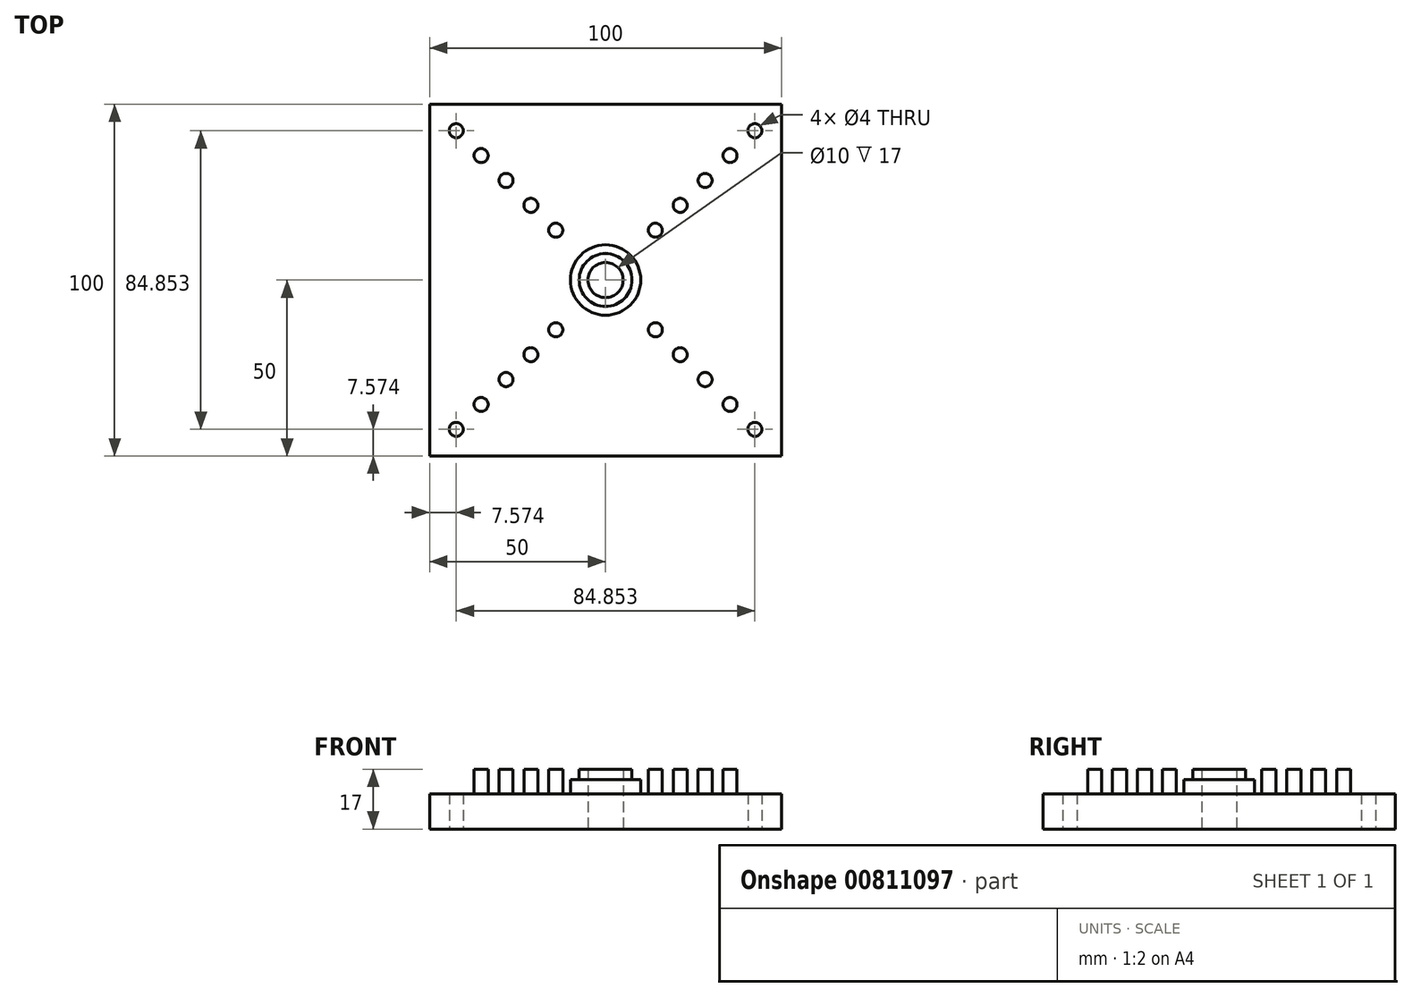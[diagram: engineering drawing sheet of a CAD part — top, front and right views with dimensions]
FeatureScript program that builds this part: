
annotation { "Feature Type Name" : "Feature", "Feature Type Description" : "" }
export const myFeature = defineFeature(function(context is Context, id is Id, definition is map)
    precondition{}
    {
        {
            var Q0;
            Q0=qCreatedBy(makeId("Top.planeOp"),FACE);
            var sketch = newSketch(context, id + "F0", { "sketchPlane" : qUnion([Q0])});
            skLineSegment(sketch, "E0.bottom", {"start": v(50, -50) * mm, "end": v(-50, -50) * mm});
            skLineSegment(sketch, "E0.top", {"start": v(50, 50) * mm, "end": v(-50, 50) * mm});
            skLineSegment(sketch, "E0.left", {"start": v(50, -50) * mm, "end": v(50, 50) * mm});
            skLineSegment(sketch, "E0.right", {"start": v(-50, -50) * mm, "end": v(-50, 50) * mm});
            skPoint(sketch, "E0.middle", {"position": v(0, 0) * mm});
            skLineSegment(sketch, "E1", {"start": v(0, 0) * mm, "end": v(42.43, -42.43) * mm, "construction": true});
            skLineSegment(sketch, "E2", {"start": v(42.43, -42.43) * mm, "end": v(50, -50) * mm, "construction": true});
            skCircle(sketch, "E3", {"center": v(42.43, -42.43) * mm, "radius": 2 * mm});
            skCircle(sketch, "E4.1.0", {"center": v(42.43, 42.43) * mm, "radius": 2 * mm});
            skCircle(sketch, "E4.2.0", {"center": v(-42.43, 42.43) * mm, "radius": 2 * mm});
            skCircle(sketch, "E4.3.0", {"center": v(-42.43, -42.43) * mm, "radius": 2 * mm});
            skSolve(sketch);
        }
        {
            var Q0;
            Q0 = qSketchRegion(id + "F0", true);
            extrude(context, id + "F1", {"entities" : qUnion([Q0]), "depth" : 10 * mm, "offsetDistance" : 25 * mm});
        }
        {
            var Q0;
            Q0=makeQuery(id+"F1.opExtrude","CAP_FACE",FACE,{"disambiguationData":[OSD([sQuery(id+"F0.wireOp",EDGE,"E0.bottom"),sQuery(id+"F0.wireOp",EDGE,"E0.top"),sQuery(id+"F0.wireOp",EDGE,"E0.left"),sQuery(id+"F0.wireOp",EDGE,"E0.right"),sQuery(id+"F0.wireOp",EDGE,"E3"),sQuery(id+"F0.wireOp",EDGE,"E4.1.0"),sQuery(id+"F0.wireOp",EDGE,"E4.2.0"),sQuery(id+"F0.wireOp",EDGE,"E4.3.0")])],"isStart":false});
            var sketch = newSketch(context, id + "F2", { "sketchPlane" : qUnion([Q0])});
            skLineSegment(sketch, "E5", {"start": v(0, 0) * mm, "end": v(14.14, -14.14) * mm, "construction": true});
            skLineSegment(sketch, "E6", {"start": v(28.28, -28.28) * mm, "end": v(35.36, -35.36) * mm, "construction": true});
            skLineSegment(sketch, "E7", {"start": v(21.21, -21.21) * mm, "end": v(28.28, -28.28) * mm, "construction": true});
            skLineSegment(sketch, "E8", {"start": v(14.14, -14.14) * mm, "end": v(21.21, -21.21) * mm, "construction": true});
            skLineSegment(sketch, "E9", {"start": v(35.36, -35.36) * mm, "end": v(42.43, -42.43) * mm, "construction": true});
            skCircle(sketch, "E10", {"center": v(14.14, -14.14) * mm, "radius": 2 * mm});
            skCircle(sketch, "E11", {"center": v(21.21, -21.21) * mm, "radius": 2 * mm});
            skCircle(sketch, "E12", {"center": v(28.28, -28.28) * mm, "radius": 2 * mm});
            skCircle(sketch, "E13", {"center": v(35.36, -35.36) * mm, "radius": 2 * mm});
            skCircle(sketch, "E14.1.0", {"center": v(14.14, 14.14) * mm, "radius": 2 * mm});
            skCircle(sketch, "E14.1.1", {"center": v(21.21, 21.21) * mm, "radius": 2 * mm});
            skCircle(sketch, "E14.1.2", {"center": v(28.28, 28.28) * mm, "radius": 2 * mm});
            skCircle(sketch, "E14.1.3", {"center": v(35.36, 35.36) * mm, "radius": 2 * mm});
            skCircle(sketch, "E14.2.0", {"center": v(-14.14, 14.14) * mm, "radius": 2 * mm});
            skCircle(sketch, "E14.2.1", {"center": v(-21.21, 21.21) * mm, "radius": 2 * mm});
            skCircle(sketch, "E14.2.2", {"center": v(-28.28, 28.28) * mm, "radius": 2 * mm});
            skCircle(sketch, "E14.2.3", {"center": v(-35.36, 35.36) * mm, "radius": 2 * mm});
            skCircle(sketch, "E14.3.0", {"center": v(-14.14, -14.14) * mm, "radius": 2 * mm});
            skCircle(sketch, "E14.3.1", {"center": v(-21.21, -21.21) * mm, "radius": 2 * mm});
            skCircle(sketch, "E14.3.2", {"center": v(-28.28, -28.28) * mm, "radius": 2 * mm});
            skCircle(sketch, "E14.3.3", {"center": v(-35.36, -35.36) * mm, "radius": 2 * mm});
            skPoint(sketch, "E14.center", {"position": v(0, 0) * mm});
            skSolve(sketch);
        }
        {
            var Q0;
            Q0 = qSketchRegion(id + "F2", true);
            extrude(context, id + "F3", {"entities" : qUnion([Q0]), "operationType" : NewBodyOperationType.ADD, "depth" : 7 * mm, "offsetDistance" : 25 * mm});
        }
        {
            var Q0;
            Q0=makeQuery(id+"F1.opExtrude","CAP_FACE",FACE,{"disambiguationData":[OSD([sQuery(id+"F0.wireOp",EDGE,"E0.bottom"),sQuery(id+"F0.wireOp",EDGE,"E0.top"),sQuery(id+"F0.wireOp",EDGE,"E0.left"),sQuery(id+"F0.wireOp",EDGE,"E0.right"),sQuery(id+"F0.wireOp",EDGE,"E3"),sQuery(id+"F0.wireOp",EDGE,"E4.1.0"),sQuery(id+"F0.wireOp",EDGE,"E4.2.0"),sQuery(id+"F0.wireOp",EDGE,"E4.3.0")])],"isStart":false});
            var sketch = newSketch(context, id + "F4", { "sketchPlane" : qUnion([Q0])});
            skCircle(sketch, "E15", {"center": v(0, 0) * mm, "radius": 10 * mm});
            skCircle(sketch, "E16", {"center": v(0, 0) * mm, "radius": 7.5 * mm});
            skCircle(sketch, "E17", {"center": v(0, 0) * mm, "radius": 5 * mm});
            skSolve(sketch);
        }
        {
            var Q0;
            Q0=makeQuery(id+"F4.imprint","IMPRINT",FACE,{"disambiguationData":[TD([[makeQuery(id+"F4.imprint","IMPRINT",EDGE,{"derivedFrom":sQuery(id+"F4.wireOp",EDGE,"E15")}),1.0]])]});
            extrude(context, id + "F5", {"entities" : qUnion([Q0]), "operationType" : NewBodyOperationType.ADD, "depth" : 4 * mm, "offsetDistance" : 25 * mm});
        }
        {
            var Q0;
            Q0=makeQuery(id+"F4.imprint","IMPRINT",FACE,{"disambiguationData":[TD([[makeQuery(id+"F4.imprint","IMPRINT",EDGE,{"derivedFrom":sQuery(id+"F4.wireOp",EDGE,"E16")}),1.0]])]});
            extrude(context, id + "F6", {"entities" : qUnion([Q0]), "operationType" : NewBodyOperationType.ADD, "depth" : 7 * mm, "offsetDistance" : 25 * mm});
        }
        {
            var Q0;
            Q0=makeQuery(id+"F4.imprint","IMPRINT",FACE,{"disambiguationData":[TD([[makeQuery(id+"F4.imprint","IMPRINT",EDGE,{"derivedFrom":sQuery(id+"F4.wireOp",EDGE,"E17")}),1.0]])]});
            extrude(context, id + "F7", {"entities" : qUnion([Q0]), "operationType" : NewBodyOperationType.REMOVE, "oppositeDirection" : true, "depth" : 25 * mm, "offsetDistance" : 25 * mm});
        }
    });
